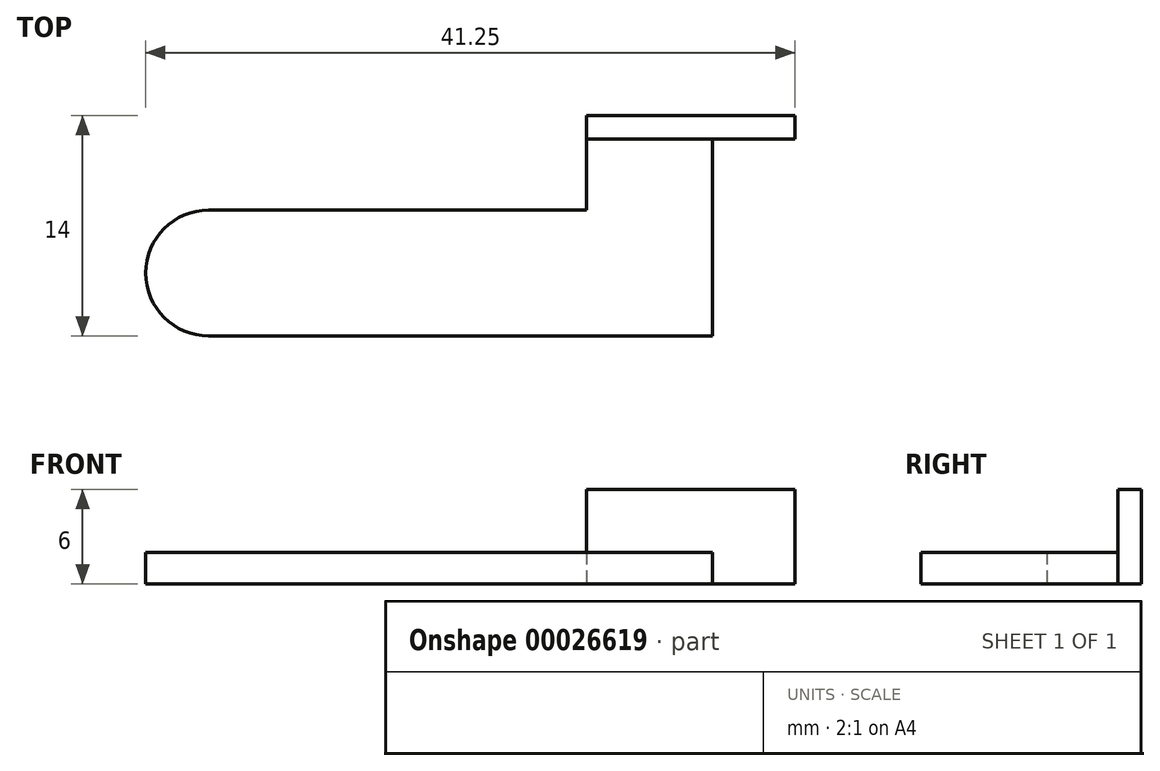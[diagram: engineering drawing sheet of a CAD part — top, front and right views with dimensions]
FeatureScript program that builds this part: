
annotation { "Feature Type Name" : "Feature", "Feature Type Description" : "" }
export const myFeature = defineFeature(function(context is Context, id is Id, definition is map)
    precondition{}
    {
        {
            var Q0;
            Q0=qCreatedBy(makeId("Top.planeOp"),FACE);
            var sketch = newSketch(context, id + "F0", { "sketchPlane" : qUnion([Q0])});
            skCircle(sketch, "E0", {"center": v(0, 0) * mm, "radius": 4 * mm});
            skLineSegment(sketch, "E1", {"start": v(0, 4) * mm, "end": v(0, -4) * mm});
            skLineSegment(sketch, "E2", {"start": v(0, -4) * mm, "end": v(32, -4) * mm});
            skLineSegment(sketch, "E3", {"start": v(32, -4) * mm, "end": v(32, 4) * mm});
            skLineSegment(sketch, "E4", {"start": v(32, 4) * mm, "end": v(0, 4) * mm});
            skLineSegment(sketch, "E5", {"start": v(32, 4) * mm, "end": v(32, 10) * mm});
            skLineSegment(sketch, "E6", {"start": v(32, 10) * mm, "end": v(24, 10) * mm});
            skLineSegment(sketch, "E7", {"start": v(24, 10) * mm, "end": v(24, 4) * mm});
            skSolve(sketch);
        }
        {
            var Q0;
            Q0 = qSketchRegion(id + "F0", true);
            extrude(context, id + "F1", {"entities" : qUnion([Q0]), "depth" : 2 * mm});
        }
        {
            var Q0;
            Q0=makeQuery(id+"F1.opExtrude","SWEPT_FACE",FACE,{"disambiguationData":[OSD([sQuery(id+"F0.wireOp",EDGE,"E3"),sQuery(id+"F0.wireOp",EDGE,"E5")])]});
            var sketch = newSketch(context, id + "F2", { "sketchPlane" : qUnion([Q0])});
            skLineSegment(sketch, "E8.bottom", {"start": v(10, 0) * mm, "end": v(8.5, 0) * mm});
            skLineSegment(sketch, "E8.top", {"start": v(10, 6) * mm, "end": v(8.5, 6) * mm});
            skLineSegment(sketch, "E8.left", {"start": v(10, 0) * mm, "end": v(10, 6) * mm});
            skLineSegment(sketch, "E8.right", {"start": v(8.5, 0) * mm, "end": v(8.5, 6) * mm});
            skSolve(sketch);
        }
        {
            var Q0;
            {var subQ5=sQuery(id+"F2.wireOp",EDGE,"E8.top");Q0=makeQuery(id+"F2.imprint","IMPRINT",FACE,{"disambiguationData":[TD([[makeQuery(id+"F2.imprint","IMPRINT",EDGE,{"derivedFrom":subQ5}),1.0]])]});}
            var Q1;
            {var subQ7=sQuery(id+"F2.wireOp",EDGE,"E8.bottom");Q1=makeQuery(id+"F2.imprint","IMPRINT",FACE,{"disambiguationData":[TD([[makeQuery(id+"F2.imprint","IMPRINT",EDGE,{"derivedFrom":subQ7}),1.0]])]});}
            extrude(context, id + "F3", {"entities" : qUnion([Q0, Q1]), "operationType" : NewBodyOperationType.ADD, "depth" : 5.25 * mm, "hasSecondDirection" : true, "secondDirectionOppositeDirection" : true, "secondDirectionDepth" : 8 * mm});
        }
    });
